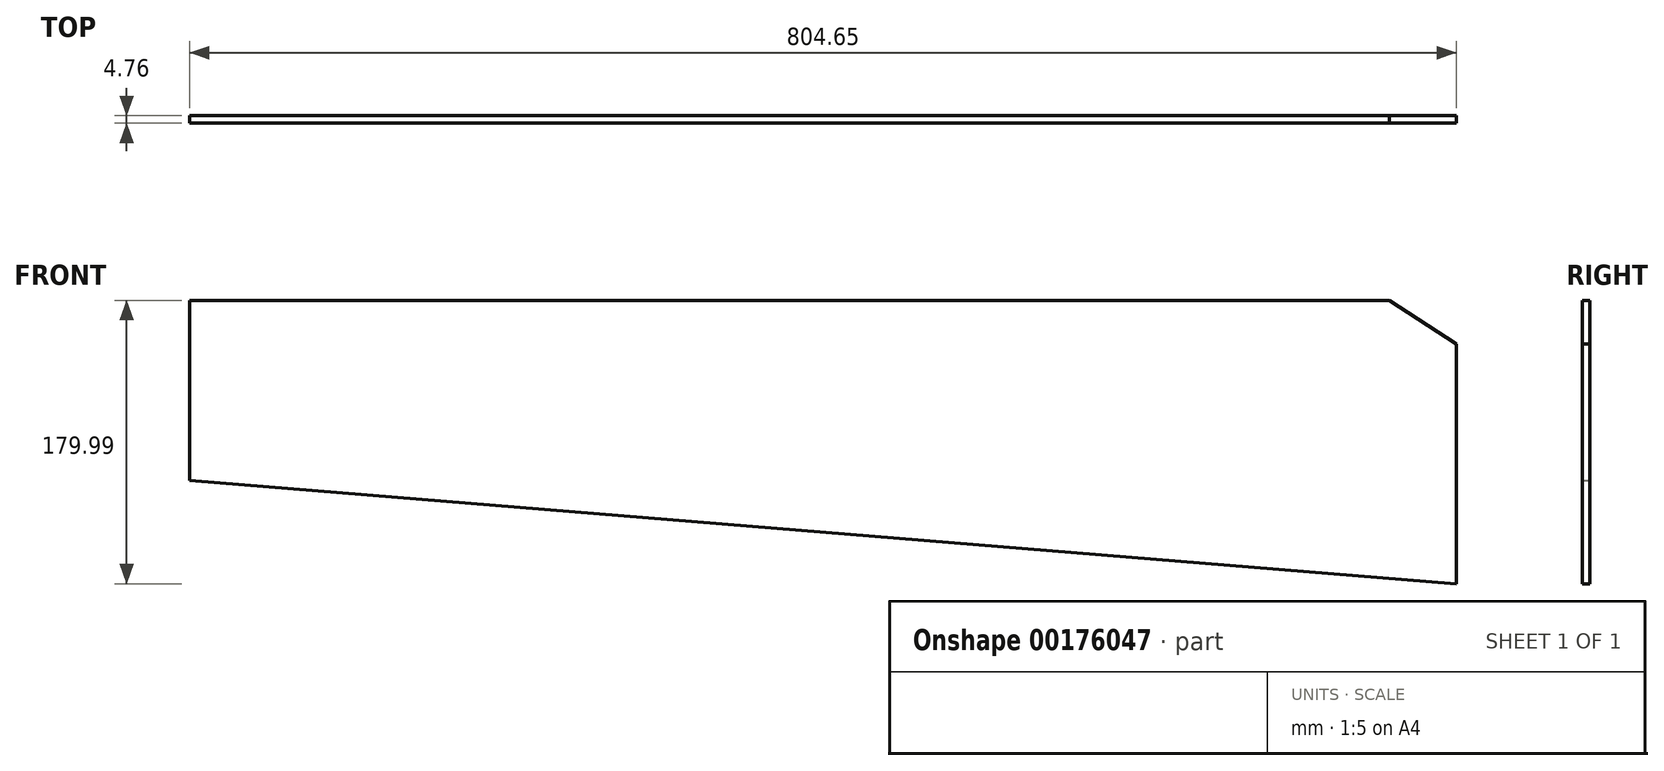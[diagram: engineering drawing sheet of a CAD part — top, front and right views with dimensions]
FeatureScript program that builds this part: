
annotation { "Feature Type Name" : "Feature", "Feature Type Description" : "" }
export const myFeature = defineFeature(function(context is Context, id is Id, definition is map)
    precondition{}
    {
        {
            var Q0;
            Q0=qCreatedBy(makeId("Front.planeOp"),FACE);
            var sketch = newSketch(context, id + "F0", { "sketchPlane" : qUnion([Q0])});
            skLineSegment(sketch, "E0", {"start": v(-254.38, 27.6) * mm, "end": v(507.62, 27.6) * mm});
            skLineSegment(sketch, "E1", {"start": v(507.62, 27.6) * mm, "end": v(550.27, 0) * mm});
            skLineSegment(sketch, "E2", {"start": v(550.27, 0) * mm, "end": v(550.27, -152.4) * mm});
            skLineSegment(sketch, "E3", {"start": v(-254.38, 27.6) * mm, "end": v(-254.38, -86.7) * mm});
            skLineSegment(sketch, "E4", {"start": v(-254.38, -86.7) * mm, "end": v(550.27, -152.4) * mm});
            skSolve(sketch);
        }
        {
            var Q0;
            Q0=makeQuery(id+"F0.imprint","IMPRINT",FACE,{"disambiguationData":[TD([[makeQuery(id+"F0.imprint","IMPRINT",EDGE,{"derivedFrom":sQuery(id+"F0.wireOp",EDGE,"E0")}),-1.0]])]});
            extrude(context, id + "F1", {"entities" : qUnion([Q0]), "depth" : 4.76 * mm});
        }
    });
